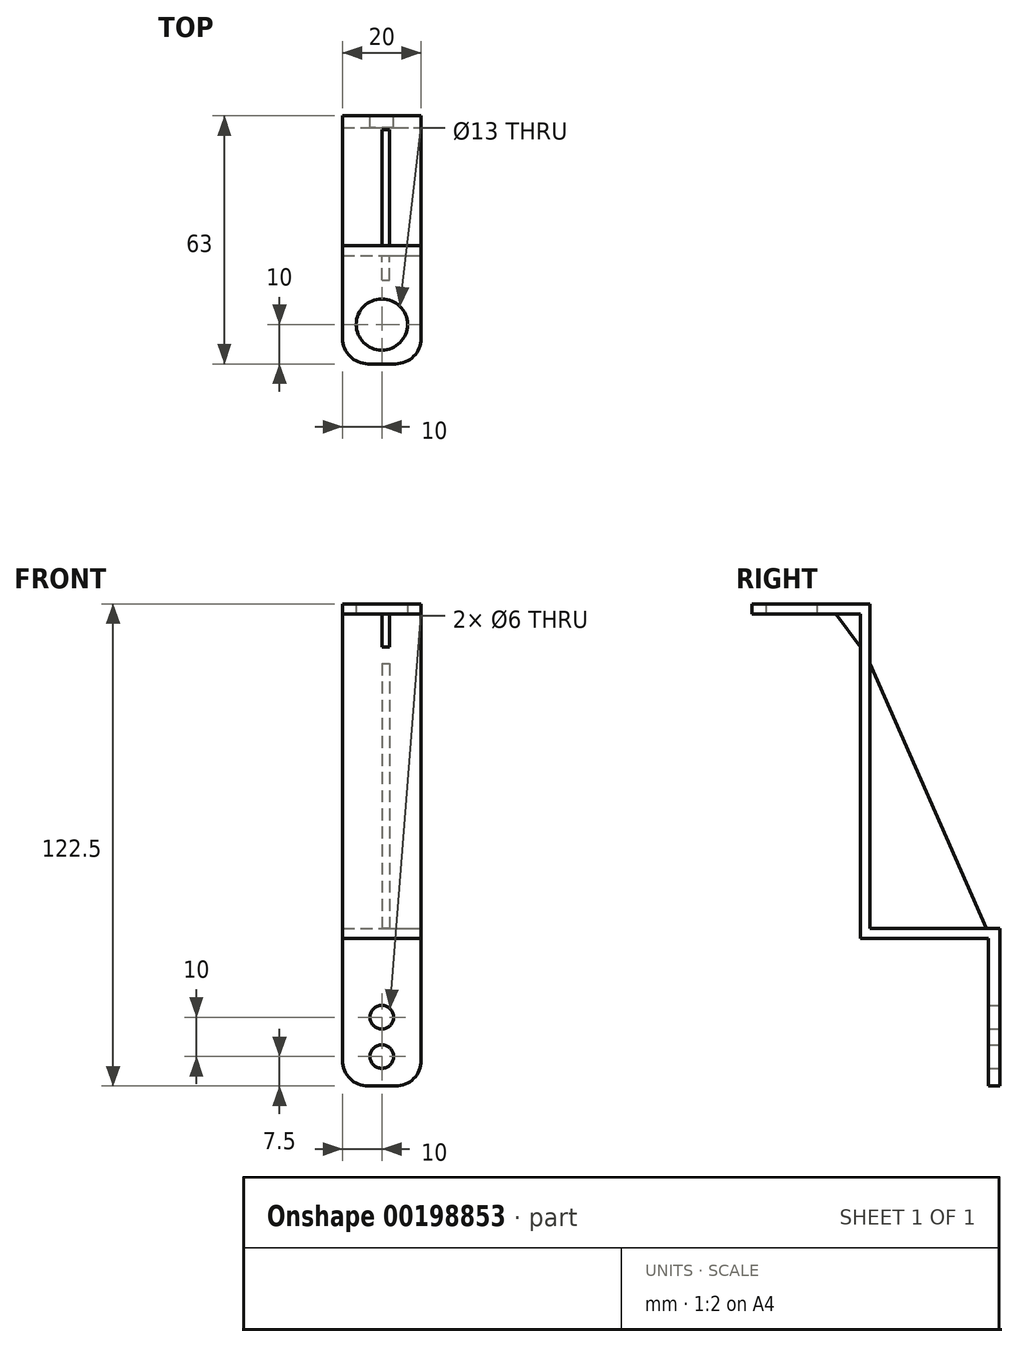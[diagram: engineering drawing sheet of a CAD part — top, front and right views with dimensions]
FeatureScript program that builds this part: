
annotation { "Feature Type Name" : "Feature", "Feature Type Description" : "" }
export const myFeature = defineFeature(function(context is Context, id is Id, definition is map)
    precondition{}
    {
        {
            var Q0;
            Q0=qCreatedBy(makeId("Front.planeOp"),FACE);
            var sketch = newSketch(context, id + "F0", { "sketchPlane" : qUnion([Q0])});
            skLineSegment(sketch, "E0.bottom", {"start": v(-10, 20) * mm, "end": v(10, 20) * mm});
            skLineSegment(sketch, "E0.top", {"start": v(-10, -20) * mm, "end": v(10, -20) * mm});
            skLineSegment(sketch, "E0.left", {"start": v(-10, 20) * mm, "end": v(-10, -20) * mm});
            skLineSegment(sketch, "E0.right", {"start": v(10, 20) * mm, "end": v(10, -20) * mm});
            skPoint(sketch, "E0.middle", {"position": v(0, 0) * mm});
            skCircle(sketch, "E1", {"center": v(0, -2.5) * mm, "radius": 3 * mm});
            skCircle(sketch, "E2", {"center": v(0, -12.5) * mm, "radius": 3 * mm});
            skSolve(sketch);
        }
        {
            var Q0;
            Q0 = qSketchRegion(id + "F0", true);
            extrude(context, id + "F1", {"entities" : qUnion([Q0]), "depth" : 3 * mm});
        }
        {
            var Q0;
            Q0=makeQuery(id+"F1.opExtrude","CAP_FACE",FACE,{"disambiguationData":[OSD([sQuery(id+"F0.wireOp",EDGE,"E0.bottom"),sQuery(id+"F0.wireOp",EDGE,"E0.top"),sQuery(id+"F0.wireOp",EDGE,"E0.left"),sQuery(id+"F0.wireOp",EDGE,"E0.right"),sQuery(id+"F0.wireOp",EDGE,"E1"),sQuery(id+"F0.wireOp",EDGE,"E2")])],"isStart":false});
            var sketch = newSketch(context, id + "F2", { "sketchPlane" : qUnion([Q0])});
            skLineSegment(sketch, "E3.bottom", {"start": v(-10, 20) * mm, "end": v(10, 20) * mm});
            skLineSegment(sketch, "E3.top", {"start": v(-10, 17.5) * mm, "end": v(10, 17.5) * mm});
            skLineSegment(sketch, "E3.left", {"start": v(-10, 20) * mm, "end": v(-10, 17.5) * mm});
            skLineSegment(sketch, "E3.right", {"start": v(10, 20) * mm, "end": v(10, 17.5) * mm});
            skSolve(sketch);
        }
        {
            var Q0;
            Q0 = qSketchRegion(id + "F2", true);
            extrude(context, id + "F3", {"entities" : qUnion([Q0]), "operationType" : NewBodyOperationType.ADD, "depth" : 32.5 * mm});
        }
        {
            var Q0;
            Q0=makeQuery(id+"F3.boolean.opBoolean","MERGE",FACE,{"derivedFrom":[makeQuery(id+"F1.opExtrude","SWEPT_FACE",FACE,{"disambiguationData":[OSD([sQuery(id+"F0.wireOp",EDGE,"E0.bottom")])]}),makeQuery(id+"F3.opExtrude","SWEPT_FACE",FACE,{"disambiguationData":[OSD([sQuery(id+"F2.wireOp",EDGE,"E3.bottom")])]})]});
            var sketch = newSketch(context, id + "F4", { "sketchPlane" : qUnion([Q0])});
            skLineSegment(sketch, "E4.bottom", {"start": v(-10, -33) * mm, "end": v(10, -33) * mm});
            skLineSegment(sketch, "E4.top", {"start": v(-10, -35.5) * mm, "end": v(10, -35.5) * mm});
            skLineSegment(sketch, "E4.left", {"start": v(-10, -33) * mm, "end": v(-10, -35.5) * mm});
            skLineSegment(sketch, "E4.right", {"start": v(10, -33) * mm, "end": v(10, -35.5) * mm});
            skSolve(sketch);
        }
        {
            var Q0;
            Q0 = qSketchRegion(id + "F4", true);
            extrude(context, id + "F5", {"entities" : qUnion([Q0]), "operationType" : NewBodyOperationType.ADD, "depth" : 80 * mm});
        }
        {
            var Q0;
            Q0=makeQuery(id+"F5.opExtrude","CAP_FACE",FACE,{"disambiguationData":[OSD([sQuery(id+"F4.wireOp",EDGE,"E4.bottom"),sQuery(id+"F4.wireOp",EDGE,"E4.top"),sQuery(id+"F4.wireOp",EDGE,"E4.left"),sQuery(id+"F4.wireOp",EDGE,"E4.right")])],"isStart":false});
            var sketch = newSketch(context, id + "F6", { "sketchPlane" : qUnion([Q0])});
            skLineSegment(sketch, "E5.bottom", {"start": v(-10, -33) * mm, "end": v(10, -33) * mm});
            skLineSegment(sketch, "E5.top", {"start": v(-10, -63) * mm, "end": v(10, -63) * mm});
            skLineSegment(sketch, "E5.left", {"start": v(-10, -33) * mm, "end": v(-10, -63) * mm});
            skLineSegment(sketch, "E5.right", {"start": v(10, -33) * mm, "end": v(10, -63) * mm});
            skCircle(sketch, "E6", {"center": v(0, -53) * mm, "radius": 6.5 * mm});
            skSolve(sketch);
        }
        {
            var Q0;
            Q0 = qSketchRegion(id + "F6", true);
            extrude(context, id + "F7", {"entities" : qUnion([Q0]), "operationType" : NewBodyOperationType.ADD, "depth" : 2.5 * mm});
        }
        {
            var Q0;
            Q0=qCreatedBy(makeId("Right.planeOp"),FACE);
            var sketch = newSketch(context, id + "F8", { "sketchPlane" : qUnion([Q0])});
            skLineSegment(sketch, "E7", {"start": v(-34.18, 101.86) * mm, "end": v(-43.08, 101.86) * mm});
            skLineSegment(sketch, "E8", {"start": v(-34.18, 101.86) * mm, "end": v(-34.18, 89.78) * mm});
            skLineSegment(sketch, "E9", {"start": v(-34.18, 89.78) * mm, "end": v(-43.08, 101.86) * mm});
            skSolve(sketch);
        }
        {
            var Q0;
            Q0 = qSketchRegion(id + "F8", true);
            extrude(context, id + "F9", {"entities" : qUnion([Q0]), "operationType" : NewBodyOperationType.ADD, "depth" : 2 * mm});
        }
        {
            var Q0;
            Q0=qCreatedBy(makeId("Right.planeOp"),FACE);
            var sketch = newSketch(context, id + "F10", { "sketchPlane" : qUnion([Q0])});
            skLineSegment(sketch, "E10", {"start": v(-34.37, 90.46) * mm, "end": v(-2.94, 18.82) * mm});
            skLineSegment(sketch, "E11", {"start": v(-2.94, 18.82) * mm, "end": v(-34.16, 18.82) * mm});
            skLineSegment(sketch, "E12", {"start": v(-34.16, 18.82) * mm, "end": v(-34.37, 90.46) * mm});
            skSolve(sketch);
        }
        {
            var Q0;
            Q0 = qSketchRegion(id + "F10", true);
            extrude(context, id + "F11", {"entities" : qUnion([Q0]), "operationType" : NewBodyOperationType.ADD, "depth" : 2 * mm});
        }
        {
            var Q0;
            Q0=makeQuery(id+"F7.opExtrude","SWEPT_EDGE",EDGE,{"disambiguationData":[OSD([sQuery(id+"F6.wireOp",EDGE,"E5.top"),sQuery(id+"F6.wireOp",EDGE,"E5.left")])]});
            var Q1;
            Q1=makeQuery(id+"F7.opExtrude","SWEPT_EDGE",EDGE,{"disambiguationData":[OSD([sQuery(id+"F6.wireOp",EDGE,"E5.top"),sQuery(id+"F6.wireOp",EDGE,"E5.right")])]});
            var Q2;
            Q2=makeQuery(id+"F1.opExtrude","SWEPT_EDGE",EDGE,{"disambiguationData":[OSD([sQuery(id+"F0.wireOp",EDGE,"E0.top"),sQuery(id+"F0.wireOp",EDGE,"E0.left")])]});
            var Q3;
            Q3=makeQuery(id+"F1.opExtrude","SWEPT_EDGE",EDGE,{"disambiguationData":[OSD([sQuery(id+"F0.wireOp",EDGE,"E0.top"),sQuery(id+"F0.wireOp",EDGE,"E0.right")])]});
            fillet(context, id + "F12", {"entities" : qUnion([Q0, Q1, Q2, Q3]), "radius" : 6.5 * mm, "tangentPropagation" : true, "allowEdgeOverflow" : false});
        }
    });
